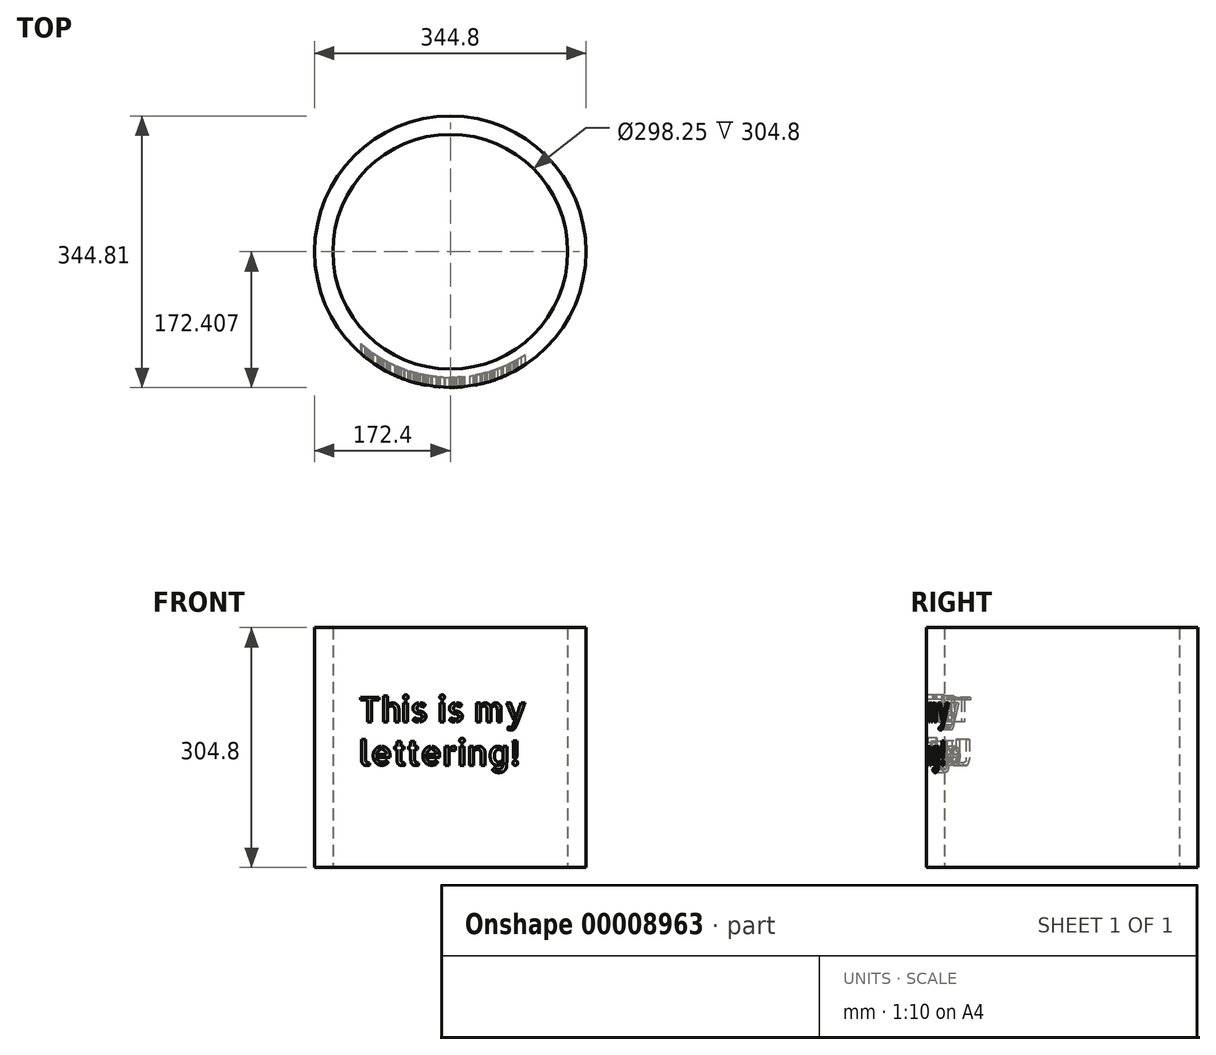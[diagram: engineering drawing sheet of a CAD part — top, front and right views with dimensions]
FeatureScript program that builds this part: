
annotation { "Feature Type Name" : "Feature", "Feature Type Description" : "" }
export const myFeature = defineFeature(function(context is Context, id is Id, definition is map)
    precondition{}
    {
        {
            var Q0;
            Q0=qCreatedBy(makeId("Top.planeOp"),FACE);
            var sketch = newSketch(context, id + "F0", { "sketchPlane" : qUnion([Q0])});
            skCircle(sketch, "E0", {"center": v(0, 214.13) * mm, "radius": 172.4 * mm});
            skCircle(sketch, "E1", {"center": v(0, 214.13) * mm, "radius": 149.13 * mm});
            skSolve(sketch);
        }
        {
            var Q0;
            Q0=makeQuery(id+"F0.imprint","IMPRINT",FACE,{"disambiguationData":[TD([[makeQuery(id+"F0.imprint","IMPRINT",EDGE,{"derivedFrom":sQuery(id+"F0.wireOp",EDGE,"E0")}),1.0]])]});
            extrude(context, id + "F1", {"entities" : qUnion([Q0]), "depth" : 304.8 * mm});
        }
        {
            var Q0;
            Q0=qCreatedBy(makeId("Front.planeOp"),FACE);
            var sketch = newSketch(context, id + "F2", { "sketchPlane" : qUnion([Q0])});
            skText(sketch, "E2", { "text": "This is my \nlettering!", "fontName": "AllertaStencil-Regular.ttf"});
            const initialGuessF2  = {"E2": [-0.11626, 0.18507, 1, 0, 0.031]};
            skSetInitialGuess(sketch, initialGuessF2);
            skSolve(sketch);
        }
        {
            var Q0;
            Q0 = qSketchRegion(id + "F2", true);
            var Q1;
            Q1=makeQuery(id+"F1.opExtrude","SWEPT_FACE",FACE,{"disambiguationData":[OSD([sQuery(id+"F0.wireOp",EDGE,"E0")])]});
            extrude(context, id + "F3", {"entities" : qUnion([Q0]), "endBound" : BoundingType.UP_TO_SURFACE, "oppositeDirection" : true, "endBoundEntityFace" : qUnion([Q1]), "depth" : 25.4 * mm});
        }
        {
            var Q0;
            Q0=makeQuery(id+"F3.opExtrude","SWEPT_BODY",BODY,{"disambiguationData":[OSD([sQuery(id+"F2.wireOp",EDGE,"E2.sketch_text.stroke-0"),sQuery(id+"F2.wireOp",EDGE,"E2.sketch_text.stroke-1"),sQuery(id+"F2.wireOp",EDGE,"E2.sketch_text.stroke-2"),sQuery(id+"F2.wireOp",EDGE,"E2.sketch_text.stroke-3"),sQuery(id+"F2.wireOp",EDGE,"E2.sketch_text.stroke-4"),sQuery(id+"F2.wireOp",EDGE,"E2.sketch_text.stroke-5"),sQuery(id+"F2.wireOp",EDGE,"E2.sketch_text.stroke-6"),sQuery(id+"F2.wireOp",EDGE,"E2.sketch_text.stroke-7")])]});
            var Q1;
            Q1=makeQuery(id+"F3.opExtrude","SWEPT_BODY",BODY,{"disambiguationData":[OSD([sQuery(id+"F2.wireOp",EDGE,"E2.sketch_text.stroke-8"),sQuery(id+"F2.wireOp",EDGE,"E2.sketch_text.stroke-9"),sQuery(id+"F2.wireOp",EDGE,"E2.sketch_text.stroke-10"),sQuery(id+"F2.wireOp",EDGE,"E2.sketch_text.stroke-11")])]});
            var Q2;
            Q2=makeQuery(id+"F3.opExtrude","SWEPT_BODY",BODY,{"disambiguationData":[OSD([sQuery(id+"F2.wireOp",EDGE,"E2.sketch_text.stroke-12"),sQuery(id+"F2.wireOp",EDGE,"E2.sketch_text.stroke-13"),sQuery(id+"F2.wireOp",EDGE,"E2.sketch_text.stroke-14"),sQuery(id+"F2.wireOp",EDGE,"E2.sketch_text.stroke-15"),sQuery(id+"F2.wireOp",EDGE,"E2.sketch_text.stroke-16"),sQuery(id+"F2.wireOp",EDGE,"E2.sketch_text.stroke-17"),sQuery(id+"F2.wireOp",EDGE,"E2.sketch_text.stroke-18"),sQuery(id+"F2.wireOp",EDGE,"E2.sketch_text.stroke-19"),sQuery(id+"F2.wireOp",EDGE,"E2.sketch_text.stroke-20"),sQuery(id+"F2.wireOp",EDGE,"E2.sketch_text.stroke-21"),sQuery(id+"F2.wireOp",EDGE,"E2.sketch_text.stroke-22"),sQuery(id+"F2.wireOp",EDGE,"E2.sketch_text.stroke-23"),sQuery(id+"F2.wireOp",EDGE,"E2.sketch_text.stroke-24"),sQuery(id+"F2.wireOp",EDGE,"E2.sketch_text.stroke-25"),sQuery(id+"F2.wireOp",EDGE,"E2.sketch_text.stroke-26"),sQuery(id+"F2.wireOp",EDGE,"E2.sketch_text.stroke-27"),sQuery(id+"F2.wireOp",EDGE,"E2.sketch_text.stroke-28"),sQuery(id+"F2.wireOp",EDGE,"E2.sketch_text.stroke-29"),sQuery(id+"F2.wireOp",EDGE,"E2.sketch_text.stroke-30")])]});
            var Q3;
            Q3=makeQuery(id+"F3.opExtrude","SWEPT_BODY",BODY,{"disambiguationData":[OSD([sQuery(id+"F2.wireOp",EDGE,"E2.sketch_text.stroke-31"),sQuery(id+"F2.wireOp",EDGE,"E2.sketch_text.stroke-32"),sQuery(id+"F2.wireOp",EDGE,"E2.sketch_text.stroke-33"),sQuery(id+"F2.wireOp",EDGE,"E2.sketch_text.stroke-34")])]});
            var Q4;
            Q4=makeQuery(id+"F3.opExtrude","SWEPT_BODY",BODY,{"disambiguationData":[OSD([sQuery(id+"F2.wireOp",EDGE,"E2.sketch_text.stroke-35"),sQuery(id+"F2.wireOp",EDGE,"E2.sketch_text.stroke-36"),sQuery(id+"F2.wireOp",EDGE,"E2.sketch_text.stroke-37"),sQuery(id+"F2.wireOp",EDGE,"E2.sketch_text.stroke-38"),sQuery(id+"F2.wireOp",EDGE,"E2.sketch_text.stroke-39"),sQuery(id+"F2.wireOp",EDGE,"E2.sketch_text.stroke-40"),sQuery(id+"F2.wireOp",EDGE,"E2.sketch_text.stroke-41"),sQuery(id+"F2.wireOp",EDGE,"E2.sketch_text.stroke-42")])]});
            var Q5;
            Q5=makeQuery(id+"F3.opExtrude","SWEPT_BODY",BODY,{"disambiguationData":[OSD([sQuery(id+"F2.wireOp",EDGE,"E2.sketch_text.stroke-43"),sQuery(id+"F2.wireOp",EDGE,"E2.sketch_text.stroke-44"),sQuery(id+"F2.wireOp",EDGE,"E2.sketch_text.stroke-45"),sQuery(id+"F2.wireOp",EDGE,"E2.sketch_text.stroke-46"),sQuery(id+"F2.wireOp",EDGE,"E2.sketch_text.stroke-47"),sQuery(id+"F2.wireOp",EDGE,"E2.sketch_text.stroke-48"),sQuery(id+"F2.wireOp",EDGE,"E2.sketch_text.stroke-49"),sQuery(id+"F2.wireOp",EDGE,"E2.sketch_text.stroke-50"),sQuery(id+"F2.wireOp",EDGE,"E2.sketch_text.stroke-51"),sQuery(id+"F2.wireOp",EDGE,"E2.sketch_text.stroke-52"),sQuery(id+"F2.wireOp",EDGE,"E2.sketch_text.stroke-53"),sQuery(id+"F2.wireOp",EDGE,"E2.sketch_text.stroke-54"),sQuery(id+"F2.wireOp",EDGE,"E2.sketch_text.stroke-55"),sQuery(id+"F2.wireOp",EDGE,"E2.sketch_text.stroke-56")])]});
            var Q6;
            Q6=makeQuery(id+"F3.opExtrude","SWEPT_BODY",BODY,{"disambiguationData":[OSD([sQuery(id+"F2.wireOp",EDGE,"E2.sketch_text.stroke-57"),sQuery(id+"F2.wireOp",EDGE,"E2.sketch_text.stroke-58"),sQuery(id+"F2.wireOp",EDGE,"E2.sketch_text.stroke-59"),sQuery(id+"F2.wireOp",EDGE,"E2.sketch_text.stroke-60"),sQuery(id+"F2.wireOp",EDGE,"E2.sketch_text.stroke-61"),sQuery(id+"F2.wireOp",EDGE,"E2.sketch_text.stroke-62")])]});
            var Q7;
            Q7=makeQuery(id+"F3.opExtrude","SWEPT_BODY",BODY,{"disambiguationData":[OSD([sQuery(id+"F2.wireOp",EDGE,"E2.sketch_text.stroke-63"),sQuery(id+"F2.wireOp",EDGE,"E2.sketch_text.stroke-64"),sQuery(id+"F2.wireOp",EDGE,"E2.sketch_text.stroke-65"),sQuery(id+"F2.wireOp",EDGE,"E2.sketch_text.stroke-66"),sQuery(id+"F2.wireOp",EDGE,"E2.sketch_text.stroke-67"),sQuery(id+"F2.wireOp",EDGE,"E2.sketch_text.stroke-68"),sQuery(id+"F2.wireOp",EDGE,"E2.sketch_text.stroke-69"),sQuery(id+"F2.wireOp",EDGE,"E2.sketch_text.stroke-70"),sQuery(id+"F2.wireOp",EDGE,"E2.sketch_text.stroke-71")])]});
            var Q8;
            Q8=makeQuery(id+"F3.opExtrude","SWEPT_BODY",BODY,{"disambiguationData":[OSD([sQuery(id+"F2.wireOp",EDGE,"E2.sketch_text.stroke-72"),sQuery(id+"F2.wireOp",EDGE,"E2.sketch_text.stroke-73"),sQuery(id+"F2.wireOp",EDGE,"E2.sketch_text.stroke-74"),sQuery(id+"F2.wireOp",EDGE,"E2.sketch_text.stroke-75"),sQuery(id+"F2.wireOp",EDGE,"E2.sketch_text.stroke-76"),sQuery(id+"F2.wireOp",EDGE,"E2.sketch_text.stroke-77"),sQuery(id+"F2.wireOp",EDGE,"E2.sketch_text.stroke-78"),sQuery(id+"F2.wireOp",EDGE,"E2.sketch_text.stroke-79"),sQuery(id+"F2.wireOp",EDGE,"E2.sketch_text.stroke-80"),sQuery(id+"F2.wireOp",EDGE,"E2.sketch_text.stroke-81"),sQuery(id+"F2.wireOp",EDGE,"E2.sketch_text.stroke-82"),sQuery(id+"F2.wireOp",EDGE,"E2.sketch_text.stroke-83"),sQuery(id+"F2.wireOp",EDGE,"E2.sketch_text.stroke-84"),sQuery(id+"F2.wireOp",EDGE,"E2.sketch_text.stroke-85")])]});
            var Q9;
            Q9=makeQuery(id+"F3.opExtrude","SWEPT_BODY",BODY,{"disambiguationData":[OSD([sQuery(id+"F2.wireOp",EDGE,"E2.sketch_text.stroke-86"),sQuery(id+"F2.wireOp",EDGE,"E2.sketch_text.stroke-87"),sQuery(id+"F2.wireOp",EDGE,"E2.sketch_text.stroke-88"),sQuery(id+"F2.wireOp",EDGE,"E2.sketch_text.stroke-89")])]});
            var Q10;
            Q10=makeQuery(id+"F3.opExtrude","SWEPT_BODY",BODY,{"disambiguationData":[OSD([sQuery(id+"F2.wireOp",EDGE,"E2.sketch_text.stroke-90"),sQuery(id+"F2.wireOp",EDGE,"E2.sketch_text.stroke-91"),sQuery(id+"F2.wireOp",EDGE,"E2.sketch_text.stroke-92"),sQuery(id+"F2.wireOp",EDGE,"E2.sketch_text.stroke-93"),sQuery(id+"F2.wireOp",EDGE,"E2.sketch_text.stroke-94"),sQuery(id+"F2.wireOp",EDGE,"E2.sketch_text.stroke-95"),sQuery(id+"F2.wireOp",EDGE,"E2.sketch_text.stroke-96"),sQuery(id+"F2.wireOp",EDGE,"E2.sketch_text.stroke-97")])]});
            var Q11;
            Q11=makeQuery(id+"F3.opExtrude","SWEPT_BODY",BODY,{"disambiguationData":[OSD([sQuery(id+"F2.wireOp",EDGE,"E2.sketch_text.stroke-98"),sQuery(id+"F2.wireOp",EDGE,"E2.sketch_text.stroke-99"),sQuery(id+"F2.wireOp",EDGE,"E2.sketch_text.stroke-100"),sQuery(id+"F2.wireOp",EDGE,"E2.sketch_text.stroke-101"),sQuery(id+"F2.wireOp",EDGE,"E2.sketch_text.stroke-102"),sQuery(id+"F2.wireOp",EDGE,"E2.sketch_text.stroke-103"),sQuery(id+"F2.wireOp",EDGE,"E2.sketch_text.stroke-104"),sQuery(id+"F2.wireOp",EDGE,"E2.sketch_text.stroke-105"),sQuery(id+"F2.wireOp",EDGE,"E2.sketch_text.stroke-106"),sQuery(id+"F2.wireOp",EDGE,"E2.sketch_text.stroke-107"),sQuery(id+"F2.wireOp",EDGE,"E2.sketch_text.stroke-108"),sQuery(id+"F2.wireOp",EDGE,"E2.sketch_text.stroke-109"),sQuery(id+"F2.wireOp",EDGE,"E2.sketch_text.stroke-110"),sQuery(id+"F2.wireOp",EDGE,"E2.sketch_text.stroke-111")])]});
            var Q12;
            Q12=makeQuery(id+"F3.opExtrude","SWEPT_BODY",BODY,{"disambiguationData":[OSD([sQuery(id+"F2.wireOp",EDGE,"E2.sketch_text.stroke-112"),sQuery(id+"F2.wireOp",EDGE,"E2.sketch_text.stroke-113"),sQuery(id+"F2.wireOp",EDGE,"E2.sketch_text.stroke-114"),sQuery(id+"F2.wireOp",EDGE,"E2.sketch_text.stroke-115"),sQuery(id+"F2.wireOp",EDGE,"E2.sketch_text.stroke-116"),sQuery(id+"F2.wireOp",EDGE,"E2.sketch_text.stroke-117")])]});
            var Q13;
            Q13=makeQuery(id+"F3.opExtrude","SWEPT_BODY",BODY,{"disambiguationData":[OSD([sQuery(id+"F2.wireOp",EDGE,"E2.sketch_text.stroke-118"),sQuery(id+"F2.wireOp",EDGE,"E2.sketch_text.stroke-119"),sQuery(id+"F2.wireOp",EDGE,"E2.sketch_text.stroke-120"),sQuery(id+"F2.wireOp",EDGE,"E2.sketch_text.stroke-121"),sQuery(id+"F2.wireOp",EDGE,"E2.sketch_text.stroke-122"),sQuery(id+"F2.wireOp",EDGE,"E2.sketch_text.stroke-123"),sQuery(id+"F2.wireOp",EDGE,"E2.sketch_text.stroke-124"),sQuery(id+"F2.wireOp",EDGE,"E2.sketch_text.stroke-125"),sQuery(id+"F2.wireOp",EDGE,"E2.sketch_text.stroke-126")])]});
            var Q14;
            Q14=makeQuery(id+"F3.opExtrude","SWEPT_BODY",BODY,{"disambiguationData":[OSD([sQuery(id+"F2.wireOp",EDGE,"E2.sketch_text.stroke-127"),sQuery(id+"F2.wireOp",EDGE,"E2.sketch_text.stroke-128"),sQuery(id+"F2.wireOp",EDGE,"E2.sketch_text.stroke-129"),sQuery(id+"F2.wireOp",EDGE,"E2.sketch_text.stroke-130"),sQuery(id+"F2.wireOp",EDGE,"E2.sketch_text.stroke-131"),sQuery(id+"F2.wireOp",EDGE,"E2.sketch_text.stroke-132"),sQuery(id+"F2.wireOp",EDGE,"E2.sketch_text.stroke-133"),sQuery(id+"F2.wireOp",EDGE,"E2.sketch_text.stroke-134"),sQuery(id+"F2.wireOp",EDGE,"E2.sketch_text.stroke-135"),sQuery(id+"F2.wireOp",EDGE,"E2.sketch_text.stroke-136"),sQuery(id+"F2.wireOp",EDGE,"E2.sketch_text.stroke-137"),sQuery(id+"F2.wireOp",EDGE,"E2.sketch_text.stroke-138"),sQuery(id+"F2.wireOp",EDGE,"E2.sketch_text.stroke-139"),sQuery(id+"F2.wireOp",EDGE,"E2.sketch_text.stroke-140")])]});
            var Q15;
            Q15=makeQuery(id+"F3.opExtrude","SWEPT_BODY",BODY,{"disambiguationData":[OSD([sQuery(id+"F2.wireOp",EDGE,"E2.sketch_text.stroke-141"),sQuery(id+"F2.wireOp",EDGE,"E2.sketch_text.stroke-142"),sQuery(id+"F2.wireOp",EDGE,"E2.sketch_text.stroke-143"),sQuery(id+"F2.wireOp",EDGE,"E2.sketch_text.stroke-144"),sQuery(id+"F2.wireOp",EDGE,"E2.sketch_text.stroke-145")])]});
            var Q16;
            Q16=makeQuery(id+"F3.opExtrude","SWEPT_BODY",BODY,{"disambiguationData":[OSD([sQuery(id+"F2.wireOp",EDGE,"E2.sketch_text.stroke-146"),sQuery(id+"F2.wireOp",EDGE,"E2.sketch_text.stroke-147"),sQuery(id+"F2.wireOp",EDGE,"E2.sketch_text.stroke-148"),sQuery(id+"F2.wireOp",EDGE,"E2.sketch_text.stroke-149"),sQuery(id+"F2.wireOp",EDGE,"E2.sketch_text.stroke-150"),sQuery(id+"F2.wireOp",EDGE,"E2.sketch_text.stroke-151"),sQuery(id+"F2.wireOp",EDGE,"E2.sketch_text.stroke-152"),sQuery(id+"F2.wireOp",EDGE,"E2.sketch_text.stroke-153"),sQuery(id+"F2.wireOp",EDGE,"E2.sketch_text.stroke-154"),sQuery(id+"F2.wireOp",EDGE,"E2.sketch_text.stroke-155"),sQuery(id+"F2.wireOp",EDGE,"E2.sketch_text.stroke-156"),sQuery(id+"F2.wireOp",EDGE,"E2.sketch_text.stroke-157"),sQuery(id+"F2.wireOp",EDGE,"E2.sketch_text.stroke-158"),sQuery(id+"F2.wireOp",EDGE,"E2.sketch_text.stroke-159"),sQuery(id+"F2.wireOp",EDGE,"E2.sketch_text.stroke-160"),sQuery(id+"F2.wireOp",EDGE,"E2.sketch_text.stroke-161")])]});
            var Q17;
            Q17=makeQuery(id+"F3.opExtrude","SWEPT_BODY",BODY,{"disambiguationData":[OSD([sQuery(id+"F2.wireOp",EDGE,"E2.sketch_text.stroke-162"),sQuery(id+"F2.wireOp",EDGE,"E2.sketch_text.stroke-163"),sQuery(id+"F2.wireOp",EDGE,"E2.sketch_text.stroke-164"),sQuery(id+"F2.wireOp",EDGE,"E2.sketch_text.stroke-165"),sQuery(id+"F2.wireOp",EDGE,"E2.sketch_text.stroke-166"),sQuery(id+"F2.wireOp",EDGE,"E2.sketch_text.stroke-167"),sQuery(id+"F2.wireOp",EDGE,"E2.sketch_text.stroke-168"),sQuery(id+"F2.wireOp",EDGE,"E2.sketch_text.stroke-169"),sQuery(id+"F2.wireOp",EDGE,"E2.sketch_text.stroke-170"),sQuery(id+"F2.wireOp",EDGE,"E2.sketch_text.stroke-171"),sQuery(id+"F2.wireOp",EDGE,"E2.sketch_text.stroke-172"),sQuery(id+"F2.wireOp",EDGE,"E2.sketch_text.stroke-173"),sQuery(id+"F2.wireOp",EDGE,"E2.sketch_text.stroke-174"),sQuery(id+"F2.wireOp",EDGE,"E2.sketch_text.stroke-175"),sQuery(id+"F2.wireOp",EDGE,"E2.sketch_text.stroke-176"),sQuery(id+"F2.wireOp",EDGE,"E2.sketch_text.stroke-177"),sQuery(id+"F2.wireOp",EDGE,"E2.sketch_text.stroke-178"),sQuery(id+"F2.wireOp",EDGE,"E2.sketch_text.stroke-179")])]});
            var Q18;
            Q18=makeQuery(id+"F3.opExtrude","SWEPT_BODY",BODY,{"disambiguationData":[OSD([sQuery(id+"F2.wireOp",EDGE,"E2.sketch_text.stroke-180"),sQuery(id+"F2.wireOp",EDGE,"E2.sketch_text.stroke-181"),sQuery(id+"F2.wireOp",EDGE,"E2.sketch_text.stroke-182"),sQuery(id+"F2.wireOp",EDGE,"E2.sketch_text.stroke-183"),sQuery(id+"F2.wireOp",EDGE,"E2.sketch_text.stroke-184"),sQuery(id+"F2.wireOp",EDGE,"E2.sketch_text.stroke-185"),sQuery(id+"F2.wireOp",EDGE,"E2.sketch_text.stroke-186"),sQuery(id+"F2.wireOp",EDGE,"E2.sketch_text.stroke-187"),sQuery(id+"F2.wireOp",EDGE,"E2.sketch_text.stroke-188"),sQuery(id+"F2.wireOp",EDGE,"E2.sketch_text.stroke-189"),sQuery(id+"F2.wireOp",EDGE,"E2.sketch_text.stroke-190"),sQuery(id+"F2.wireOp",EDGE,"E2.sketch_text.stroke-191"),sQuery(id+"F2.wireOp",EDGE,"E2.sketch_text.stroke-192"),sQuery(id+"F2.wireOp",EDGE,"E2.sketch_text.stroke-193"),sQuery(id+"F2.wireOp",EDGE,"E2.sketch_text.stroke-194"),sQuery(id+"F2.wireOp",EDGE,"E2.sketch_text.stroke-195"),sQuery(id+"F2.wireOp",EDGE,"E2.sketch_text.stroke-196"),sQuery(id+"F2.wireOp",EDGE,"E2.sketch_text.stroke-197"),sQuery(id+"F2.wireOp",EDGE,"E2.sketch_text.stroke-198"),sQuery(id+"F2.wireOp",EDGE,"E2.sketch_text.stroke-199"),sQuery(id+"F2.wireOp",EDGE,"E2.sketch_text.stroke-200"),sQuery(id+"F2.wireOp",EDGE,"E2.sketch_text.stroke-201"),sQuery(id+"F2.wireOp",EDGE,"E2.sketch_text.stroke-202"),sQuery(id+"F2.wireOp",EDGE,"E2.sketch_text.stroke-203")])]});
            var Q19;
            Q19=makeQuery(id+"F3.opExtrude","SWEPT_BODY",BODY,{"disambiguationData":[OSD([sQuery(id+"F2.wireOp",EDGE,"E2.sketch_text.stroke-204"),sQuery(id+"F2.wireOp",EDGE,"E2.sketch_text.stroke-205"),sQuery(id+"F2.wireOp",EDGE,"E2.sketch_text.stroke-206"),sQuery(id+"F2.wireOp",EDGE,"E2.sketch_text.stroke-207"),sQuery(id+"F2.wireOp",EDGE,"E2.sketch_text.stroke-208")])]});
            var Q20;
            Q20=makeQuery(id+"F3.opExtrude","SWEPT_BODY",BODY,{"disambiguationData":[OSD([sQuery(id+"F2.wireOp",EDGE,"E2.sketch_text.stroke-209"),sQuery(id+"F2.wireOp",EDGE,"E2.sketch_text.stroke-210"),sQuery(id+"F2.wireOp",EDGE,"E2.sketch_text.stroke-211"),sQuery(id+"F2.wireOp",EDGE,"E2.sketch_text.stroke-212"),sQuery(id+"F2.wireOp",EDGE,"E2.sketch_text.stroke-213"),sQuery(id+"F2.wireOp",EDGE,"E2.sketch_text.stroke-214"),sQuery(id+"F2.wireOp",EDGE,"E2.sketch_text.stroke-215"),sQuery(id+"F2.wireOp",EDGE,"E2.sketch_text.stroke-216"),sQuery(id+"F2.wireOp",EDGE,"E2.sketch_text.stroke-217"),sQuery(id+"F2.wireOp",EDGE,"E2.sketch_text.stroke-218"),sQuery(id+"F2.wireOp",EDGE,"E2.sketch_text.stroke-219"),sQuery(id+"F2.wireOp",EDGE,"E2.sketch_text.stroke-220"),sQuery(id+"F2.wireOp",EDGE,"E2.sketch_text.stroke-221"),sQuery(id+"F2.wireOp",EDGE,"E2.sketch_text.stroke-222"),sQuery(id+"F2.wireOp",EDGE,"E2.sketch_text.stroke-223"),sQuery(id+"F2.wireOp",EDGE,"E2.sketch_text.stroke-224"),sQuery(id+"F2.wireOp",EDGE,"E2.sketch_text.stroke-225"),sQuery(id+"F2.wireOp",EDGE,"E2.sketch_text.stroke-226")])]});
            var Q21;
            Q21=makeQuery(id+"F3.opExtrude","SWEPT_BODY",BODY,{"disambiguationData":[OSD([sQuery(id+"F2.wireOp",EDGE,"E2.sketch_text.stroke-227"),sQuery(id+"F2.wireOp",EDGE,"E2.sketch_text.stroke-228"),sQuery(id+"F2.wireOp",EDGE,"E2.sketch_text.stroke-229"),sQuery(id+"F2.wireOp",EDGE,"E2.sketch_text.stroke-230"),sQuery(id+"F2.wireOp",EDGE,"E2.sketch_text.stroke-231"),sQuery(id+"F2.wireOp",EDGE,"E2.sketch_text.stroke-232"),sQuery(id+"F2.wireOp",EDGE,"E2.sketch_text.stroke-233"),sQuery(id+"F2.wireOp",EDGE,"E2.sketch_text.stroke-234"),sQuery(id+"F2.wireOp",EDGE,"E2.sketch_text.stroke-235"),sQuery(id+"F2.wireOp",EDGE,"E2.sketch_text.stroke-236"),sQuery(id+"F2.wireOp",EDGE,"E2.sketch_text.stroke-237"),sQuery(id+"F2.wireOp",EDGE,"E2.sketch_text.stroke-238"),sQuery(id+"F2.wireOp",EDGE,"E2.sketch_text.stroke-239")])]});
            var Q22;
            Q22=makeQuery(id+"F3.opExtrude","SWEPT_BODY",BODY,{"disambiguationData":[OSD([sQuery(id+"F2.wireOp",EDGE,"E2.sketch_text.stroke-240"),sQuery(id+"F2.wireOp",EDGE,"E2.sketch_text.stroke-241"),sQuery(id+"F2.wireOp",EDGE,"E2.sketch_text.stroke-242"),sQuery(id+"F2.wireOp",EDGE,"E2.sketch_text.stroke-243"),sQuery(id+"F2.wireOp",EDGE,"E2.sketch_text.stroke-244"),sQuery(id+"F2.wireOp",EDGE,"E2.sketch_text.stroke-245"),sQuery(id+"F2.wireOp",EDGE,"E2.sketch_text.stroke-246"),sQuery(id+"F2.wireOp",EDGE,"E2.sketch_text.stroke-247"),sQuery(id+"F2.wireOp",EDGE,"E2.sketch_text.stroke-248"),sQuery(id+"F2.wireOp",EDGE,"E2.sketch_text.stroke-249"),sQuery(id+"F2.wireOp",EDGE,"E2.sketch_text.stroke-250"),sQuery(id+"F2.wireOp",EDGE,"E2.sketch_text.stroke-251"),sQuery(id+"F2.wireOp",EDGE,"E2.sketch_text.stroke-252"),sQuery(id+"F2.wireOp",EDGE,"E2.sketch_text.stroke-253"),sQuery(id+"F2.wireOp",EDGE,"E2.sketch_text.stroke-254"),sQuery(id+"F2.wireOp",EDGE,"E2.sketch_text.stroke-255"),sQuery(id+"F2.wireOp",EDGE,"E2.sketch_text.stroke-256"),sQuery(id+"F2.wireOp",EDGE,"E2.sketch_text.stroke-257"),sQuery(id+"F2.wireOp",EDGE,"E2.sketch_text.stroke-258"),sQuery(id+"F2.wireOp",EDGE,"E2.sketch_text.stroke-259"),sQuery(id+"F2.wireOp",EDGE,"E2.sketch_text.stroke-260"),sQuery(id+"F2.wireOp",EDGE,"E2.sketch_text.stroke-261"),sQuery(id+"F2.wireOp",EDGE,"E2.sketch_text.stroke-262"),sQuery(id+"F2.wireOp",EDGE,"E2.sketch_text.stroke-263")])]});
            var Q23;
            Q23=makeQuery(id+"F3.opExtrude","SWEPT_BODY",BODY,{"disambiguationData":[OSD([sQuery(id+"F2.wireOp",EDGE,"E2.sketch_text.stroke-264"),sQuery(id+"F2.wireOp",EDGE,"E2.sketch_text.stroke-265"),sQuery(id+"F2.wireOp",EDGE,"E2.sketch_text.stroke-266"),sQuery(id+"F2.wireOp",EDGE,"E2.sketch_text.stroke-267"),sQuery(id+"F2.wireOp",EDGE,"E2.sketch_text.stroke-268"),sQuery(id+"F2.wireOp",EDGE,"E2.sketch_text.stroke-269"),sQuery(id+"F2.wireOp",EDGE,"E2.sketch_text.stroke-270"),sQuery(id+"F2.wireOp",EDGE,"E2.sketch_text.stroke-271"),sQuery(id+"F2.wireOp",EDGE,"E2.sketch_text.stroke-272"),sQuery(id+"F2.wireOp",EDGE,"E2.sketch_text.stroke-273"),sQuery(id+"F2.wireOp",EDGE,"E2.sketch_text.stroke-274"),sQuery(id+"F2.wireOp",EDGE,"E2.sketch_text.stroke-275"),sQuery(id+"F2.wireOp",EDGE,"E2.sketch_text.stroke-276"),sQuery(id+"F2.wireOp",EDGE,"E2.sketch_text.stroke-277"),sQuery(id+"F2.wireOp",EDGE,"E2.sketch_text.stroke-278"),sQuery(id+"F2.wireOp",EDGE,"E2.sketch_text.stroke-279"),sQuery(id+"F2.wireOp",EDGE,"E2.sketch_text.stroke-280"),sQuery(id+"F2.wireOp",EDGE,"E2.sketch_text.stroke-281"),sQuery(id+"F2.wireOp",EDGE,"E2.sketch_text.stroke-282"),sQuery(id+"F2.wireOp",EDGE,"E2.sketch_text.stroke-283"),sQuery(id+"F2.wireOp",EDGE,"E2.sketch_text.stroke-284"),sQuery(id+"F2.wireOp",EDGE,"E2.sketch_text.stroke-285"),sQuery(id+"F2.wireOp",EDGE,"E2.sketch_text.stroke-286"),sQuery(id+"F2.wireOp",EDGE,"E2.sketch_text.stroke-287"),sQuery(id+"F2.wireOp",EDGE,"E2.sketch_text.stroke-288")])]});
            var Q24;
            Q24=makeQuery(id+"F3.opExtrude","SWEPT_BODY",BODY,{"disambiguationData":[OSD([sQuery(id+"F2.wireOp",EDGE,"E2.sketch_text.stroke-289"),sQuery(id+"F2.wireOp",EDGE,"E2.sketch_text.stroke-290"),sQuery(id+"F2.wireOp",EDGE,"E2.sketch_text.stroke-291"),sQuery(id+"F2.wireOp",EDGE,"E2.sketch_text.stroke-292"),sQuery(id+"F2.wireOp",EDGE,"E2.sketch_text.stroke-293"),sQuery(id+"F2.wireOp",EDGE,"E2.sketch_text.stroke-294"),sQuery(id+"F2.wireOp",EDGE,"E2.sketch_text.stroke-295"),sQuery(id+"F2.wireOp",EDGE,"E2.sketch_text.stroke-296"),sQuery(id+"F2.wireOp",EDGE,"E2.sketch_text.stroke-297"),sQuery(id+"F2.wireOp",EDGE,"E2.sketch_text.stroke-298"),sQuery(id+"F2.wireOp",EDGE,"E2.sketch_text.stroke-299"),sQuery(id+"F2.wireOp",EDGE,"E2.sketch_text.stroke-300"),sQuery(id+"F2.wireOp",EDGE,"E2.sketch_text.stroke-301"),sQuery(id+"F2.wireOp",EDGE,"E2.sketch_text.stroke-302"),sQuery(id+"F2.wireOp",EDGE,"E2.sketch_text.stroke-303"),sQuery(id+"F2.wireOp",EDGE,"E2.sketch_text.stroke-304"),sQuery(id+"F2.wireOp",EDGE,"E2.sketch_text.stroke-305"),sQuery(id+"F2.wireOp",EDGE,"E2.sketch_text.stroke-306"),sQuery(id+"F2.wireOp",EDGE,"E2.sketch_text.stroke-307"),sQuery(id+"F2.wireOp",EDGE,"E2.sketch_text.stroke-308"),sQuery(id+"F2.wireOp",EDGE,"E2.sketch_text.stroke-309"),sQuery(id+"F2.wireOp",EDGE,"E2.sketch_text.stroke-310"),sQuery(id+"F2.wireOp",EDGE,"E2.sketch_text.stroke-311"),sQuery(id+"F2.wireOp",EDGE,"E2.sketch_text.stroke-312"),sQuery(id+"F2.wireOp",EDGE,"E2.sketch_text.stroke-313")])]});
            var Q25;
            Q25=makeQuery(id+"F3.opExtrude","SWEPT_BODY",BODY,{"disambiguationData":[OSD([sQuery(id+"F2.wireOp",EDGE,"E2.sketch_text.stroke-314"),sQuery(id+"F2.wireOp",EDGE,"E2.sketch_text.stroke-315"),sQuery(id+"F2.wireOp",EDGE,"E2.sketch_text.stroke-316"),sQuery(id+"F2.wireOp",EDGE,"E2.sketch_text.stroke-317"),sQuery(id+"F2.wireOp",EDGE,"E2.sketch_text.stroke-318"),sQuery(id+"F2.wireOp",EDGE,"E2.sketch_text.stroke-319"),sQuery(id+"F2.wireOp",EDGE,"E2.sketch_text.stroke-320"),sQuery(id+"F2.wireOp",EDGE,"E2.sketch_text.stroke-321"),sQuery(id+"F2.wireOp",EDGE,"E2.sketch_text.stroke-322"),sQuery(id+"F2.wireOp",EDGE,"E2.sketch_text.stroke-323"),sQuery(id+"F2.wireOp",EDGE,"E2.sketch_text.stroke-324"),sQuery(id+"F2.wireOp",EDGE,"E2.sketch_text.stroke-325"),sQuery(id+"F2.wireOp",EDGE,"E2.sketch_text.stroke-326")])]});
            var Q26;
            Q26=makeQuery(id+"F3.opExtrude","SWEPT_BODY",BODY,{"disambiguationData":[OSD([sQuery(id+"F2.wireOp",EDGE,"E2.sketch_text.stroke-327"),sQuery(id+"F2.wireOp",EDGE,"E2.sketch_text.stroke-328"),sQuery(id+"F2.wireOp",EDGE,"E2.sketch_text.stroke-329"),sQuery(id+"F2.wireOp",EDGE,"E2.sketch_text.stroke-330"),sQuery(id+"F2.wireOp",EDGE,"E2.sketch_text.stroke-331"),sQuery(id+"F2.wireOp",EDGE,"E2.sketch_text.stroke-332"),sQuery(id+"F2.wireOp",EDGE,"E2.sketch_text.stroke-333"),sQuery(id+"F2.wireOp",EDGE,"E2.sketch_text.stroke-334"),sQuery(id+"F2.wireOp",EDGE,"E2.sketch_text.stroke-335"),sQuery(id+"F2.wireOp",EDGE,"E2.sketch_text.stroke-336"),sQuery(id+"F2.wireOp",EDGE,"E2.sketch_text.stroke-337"),sQuery(id+"F2.wireOp",EDGE,"E2.sketch_text.stroke-338"),sQuery(id+"F2.wireOp",EDGE,"E2.sketch_text.stroke-339"),sQuery(id+"F2.wireOp",EDGE,"E2.sketch_text.stroke-340"),sQuery(id+"F2.wireOp",EDGE,"E2.sketch_text.stroke-341"),sQuery(id+"F2.wireOp",EDGE,"E2.sketch_text.stroke-342"),sQuery(id+"F2.wireOp",EDGE,"E2.sketch_text.stroke-343"),sQuery(id+"F2.wireOp",EDGE,"E2.sketch_text.stroke-344"),sQuery(id+"F2.wireOp",EDGE,"E2.sketch_text.stroke-345"),sQuery(id+"F2.wireOp",EDGE,"E2.sketch_text.stroke-346"),sQuery(id+"F2.wireOp",EDGE,"E2.sketch_text.stroke-347"),sQuery(id+"F2.wireOp",EDGE,"E2.sketch_text.stroke-348"),sQuery(id+"F2.wireOp",EDGE,"E2.sketch_text.stroke-349"),sQuery(id+"F2.wireOp",EDGE,"E2.sketch_text.stroke-350")])]});
            var Q27;
            Q27=makeQuery(id+"F3.opExtrude","SWEPT_BODY",BODY,{"disambiguationData":[OSD([sQuery(id+"F2.wireOp",EDGE,"E2.sketch_text.stroke-351"),sQuery(id+"F2.wireOp",EDGE,"E2.sketch_text.stroke-352"),sQuery(id+"F2.wireOp",EDGE,"E2.sketch_text.stroke-353"),sQuery(id+"F2.wireOp",EDGE,"E2.sketch_text.stroke-354"),sQuery(id+"F2.wireOp",EDGE,"E2.sketch_text.stroke-355"),sQuery(id+"F2.wireOp",EDGE,"E2.sketch_text.stroke-356"),sQuery(id+"F2.wireOp",EDGE,"E2.sketch_text.stroke-357")])]});
            var Q28;
            Q28=makeQuery(id+"F3.opExtrude","SWEPT_BODY",BODY,{"disambiguationData":[OSD([sQuery(id+"F2.wireOp",EDGE,"E2.sketch_text.stroke-358"),sQuery(id+"F2.wireOp",EDGE,"E2.sketch_text.stroke-359"),sQuery(id+"F2.wireOp",EDGE,"E2.sketch_text.stroke-360"),sQuery(id+"F2.wireOp",EDGE,"E2.sketch_text.stroke-361"),sQuery(id+"F2.wireOp",EDGE,"E2.sketch_text.stroke-362"),sQuery(id+"F2.wireOp",EDGE,"E2.sketch_text.stroke-363"),sQuery(id+"F2.wireOp",EDGE,"E2.sketch_text.stroke-364")])]});
            var Q29;
            Q29=makeQuery(id+"F3.opExtrude","SWEPT_BODY",BODY,{"disambiguationData":[OSD([sQuery(id+"F2.wireOp",EDGE,"E2.sketch_text.stroke-365"),sQuery(id+"F2.wireOp",EDGE,"E2.sketch_text.stroke-366"),sQuery(id+"F2.wireOp",EDGE,"E2.sketch_text.stroke-367"),sQuery(id+"F2.wireOp",EDGE,"E2.sketch_text.stroke-368")])]});
            var Q30;
            Q30=makeQuery(id+"F3.opExtrude","SWEPT_BODY",BODY,{"disambiguationData":[OSD([sQuery(id+"F2.wireOp",EDGE,"E2.sketch_text.stroke-369"),sQuery(id+"F2.wireOp",EDGE,"E2.sketch_text.stroke-370"),sQuery(id+"F2.wireOp",EDGE,"E2.sketch_text.stroke-371"),sQuery(id+"F2.wireOp",EDGE,"E2.sketch_text.stroke-372"),sQuery(id+"F2.wireOp",EDGE,"E2.sketch_text.stroke-373"),sQuery(id+"F2.wireOp",EDGE,"E2.sketch_text.stroke-374"),sQuery(id+"F2.wireOp",EDGE,"E2.sketch_text.stroke-375"),sQuery(id+"F2.wireOp",EDGE,"E2.sketch_text.stroke-376")])]});
            var Q31;
            Q31=makeQuery(id+"F3.opExtrude","SWEPT_BODY",BODY,{"disambiguationData":[OSD([sQuery(id+"F2.wireOp",EDGE,"E2.sketch_text.stroke-377"),sQuery(id+"F2.wireOp",EDGE,"E2.sketch_text.stroke-378"),sQuery(id+"F2.wireOp",EDGE,"E2.sketch_text.stroke-379"),sQuery(id+"F2.wireOp",EDGE,"E2.sketch_text.stroke-380"),sQuery(id+"F2.wireOp",EDGE,"E2.sketch_text.stroke-381")])]});
            var Q32;
            Q32=makeQuery(id+"F3.opExtrude","SWEPT_BODY",BODY,{"disambiguationData":[OSD([sQuery(id+"F2.wireOp",EDGE,"E2.sketch_text.stroke-382"),sQuery(id+"F2.wireOp",EDGE,"E2.sketch_text.stroke-383"),sQuery(id+"F2.wireOp",EDGE,"E2.sketch_text.stroke-384"),sQuery(id+"F2.wireOp",EDGE,"E2.sketch_text.stroke-385"),sQuery(id+"F2.wireOp",EDGE,"E2.sketch_text.stroke-386"),sQuery(id+"F2.wireOp",EDGE,"E2.sketch_text.stroke-387"),sQuery(id+"F2.wireOp",EDGE,"E2.sketch_text.stroke-388"),sQuery(id+"F2.wireOp",EDGE,"E2.sketch_text.stroke-389"),sQuery(id+"F2.wireOp",EDGE,"E2.sketch_text.stroke-390"),sQuery(id+"F2.wireOp",EDGE,"E2.sketch_text.stroke-391"),sQuery(id+"F2.wireOp",EDGE,"E2.sketch_text.stroke-392"),sQuery(id+"F2.wireOp",EDGE,"E2.sketch_text.stroke-393"),sQuery(id+"F2.wireOp",EDGE,"E2.sketch_text.stroke-394"),sQuery(id+"F2.wireOp",EDGE,"E2.sketch_text.stroke-395"),sQuery(id+"F2.wireOp",EDGE,"E2.sketch_text.stroke-396"),sQuery(id+"F2.wireOp",EDGE,"E2.sketch_text.stroke-397"),sQuery(id+"F2.wireOp",EDGE,"E2.sketch_text.stroke-398"),sQuery(id+"F2.wireOp",EDGE,"E2.sketch_text.stroke-399"),sQuery(id+"F2.wireOp",EDGE,"E2.sketch_text.stroke-400")])]});
            var Q33;
            Q33=makeQuery(id+"F3.opExtrude","SWEPT_BODY",BODY,{"disambiguationData":[OSD([sQuery(id+"F2.wireOp",EDGE,"E2.sketch_text.stroke-401"),sQuery(id+"F2.wireOp",EDGE,"E2.sketch_text.stroke-402"),sQuery(id+"F2.wireOp",EDGE,"E2.sketch_text.stroke-403"),sQuery(id+"F2.wireOp",EDGE,"E2.sketch_text.stroke-404"),sQuery(id+"F2.wireOp",EDGE,"E2.sketch_text.stroke-405"),sQuery(id+"F2.wireOp",EDGE,"E2.sketch_text.stroke-406"),sQuery(id+"F2.wireOp",EDGE,"E2.sketch_text.stroke-407"),sQuery(id+"F2.wireOp",EDGE,"E2.sketch_text.stroke-408"),sQuery(id+"F2.wireOp",EDGE,"E2.sketch_text.stroke-409"),sQuery(id+"F2.wireOp",EDGE,"E2.sketch_text.stroke-410"),sQuery(id+"F2.wireOp",EDGE,"E2.sketch_text.stroke-411"),sQuery(id+"F2.wireOp",EDGE,"E2.sketch_text.stroke-412"),sQuery(id+"F2.wireOp",EDGE,"E2.sketch_text.stroke-413"),sQuery(id+"F2.wireOp",EDGE,"E2.sketch_text.stroke-414"),sQuery(id+"F2.wireOp",EDGE,"E2.sketch_text.stroke-415"),sQuery(id+"F2.wireOp",EDGE,"E2.sketch_text.stroke-416"),sQuery(id+"F2.wireOp",EDGE,"E2.sketch_text.stroke-417"),sQuery(id+"F2.wireOp",EDGE,"E2.sketch_text.stroke-418"),sQuery(id+"F2.wireOp",EDGE,"E2.sketch_text.stroke-419"),sQuery(id+"F2.wireOp",EDGE,"E2.sketch_text.stroke-420"),sQuery(id+"F2.wireOp",EDGE,"E2.sketch_text.stroke-421"),sQuery(id+"F2.wireOp",EDGE,"E2.sketch_text.stroke-422"),sQuery(id+"F2.wireOp",EDGE,"E2.sketch_text.stroke-423"),sQuery(id+"F2.wireOp",EDGE,"E2.sketch_text.stroke-424"),sQuery(id+"F2.wireOp",EDGE,"E2.sketch_text.stroke-425"),sQuery(id+"F2.wireOp",EDGE,"E2.sketch_text.stroke-426")])]});
            var Q34;
            Q34=makeQuery(id+"F3.opExtrude","SWEPT_BODY",BODY,{"disambiguationData":[OSD([sQuery(id+"F2.wireOp",EDGE,"E2.sketch_text.stroke-427"),sQuery(id+"F2.wireOp",EDGE,"E2.sketch_text.stroke-428"),sQuery(id+"F2.wireOp",EDGE,"E2.sketch_text.stroke-429"),sQuery(id+"F2.wireOp",EDGE,"E2.sketch_text.stroke-430"),sQuery(id+"F2.wireOp",EDGE,"E2.sketch_text.stroke-431"),sQuery(id+"F2.wireOp",EDGE,"E2.sketch_text.stroke-432"),sQuery(id+"F2.wireOp",EDGE,"E2.sketch_text.stroke-433"),sQuery(id+"F2.wireOp",EDGE,"E2.sketch_text.stroke-434"),sQuery(id+"F2.wireOp",EDGE,"E2.sketch_text.stroke-435"),sQuery(id+"F2.wireOp",EDGE,"E2.sketch_text.stroke-436"),sQuery(id+"F2.wireOp",EDGE,"E2.sketch_text.stroke-437"),sQuery(id+"F2.wireOp",EDGE,"E2.sketch_text.stroke-438"),sQuery(id+"F2.wireOp",EDGE,"E2.sketch_text.stroke-439"),sQuery(id+"F2.wireOp",EDGE,"E2.sketch_text.stroke-440"),sQuery(id+"F2.wireOp",EDGE,"E2.sketch_text.stroke-441"),sQuery(id+"F2.wireOp",EDGE,"E2.sketch_text.stroke-442"),sQuery(id+"F2.wireOp",EDGE,"E2.sketch_text.stroke-443")])]});
            var Q35;
            Q35=makeQuery(id+"F3.opExtrude","SWEPT_BODY",BODY,{"disambiguationData":[OSD([sQuery(id+"F2.wireOp",EDGE,"E2.sketch_text.stroke-444"),sQuery(id+"F2.wireOp",EDGE,"E2.sketch_text.stroke-445"),sQuery(id+"F2.wireOp",EDGE,"E2.sketch_text.stroke-446"),sQuery(id+"F2.wireOp",EDGE,"E2.sketch_text.stroke-447")])]});
            var Q36;
            Q36=makeQuery(id+"F3.opExtrude","SWEPT_BODY",BODY,{"disambiguationData":[OSD([sQuery(id+"F2.wireOp",EDGE,"E2.sketch_text.stroke-448"),sQuery(id+"F2.wireOp",EDGE,"E2.sketch_text.stroke-449"),sQuery(id+"F2.wireOp",EDGE,"E2.sketch_text.stroke-450"),sQuery(id+"F2.wireOp",EDGE,"E2.sketch_text.stroke-451"),sQuery(id+"F2.wireOp",EDGE,"E2.sketch_text.stroke-452"),sQuery(id+"F2.wireOp",EDGE,"E2.sketch_text.stroke-453"),sQuery(id+"F2.wireOp",EDGE,"E2.sketch_text.stroke-454"),sQuery(id+"F2.wireOp",EDGE,"E2.sketch_text.stroke-455")])]});
            var Q37;
            Q37=qCreatedBy(makeId("Front.planeOp"),FACE);
            transform(context, id + "F4", {"entities" : qUnion([Q0, Q1, Q2, Q3, Q4, Q5, Q6, Q7, Q8, Q9, Q10, Q11, Q12, Q13, Q14, Q15, Q16, Q17, Q18, Q19, Q20, Q21, Q22, Q23, Q24, Q25, Q26, Q27, Q28, Q29, Q30, Q31, Q32, Q33, Q34, Q35, Q36]), "transformType" : TransformType.TRANSLATION_DISTANCE, "transformDirection" : qUnion([Q37]), "distance" : 12.7 * mm, "oppositeDirection" : true, "makeCopy" : false});
        }
        {
            var Q0;
            Q0=makeQuery(id+"F3.opExtrude","SWEPT_BODY",BODY,{"disambiguationData":[OSD([sQuery(id+"F2.wireOp",EDGE,"E2.sketch_text.stroke-0"),sQuery(id+"F2.wireOp",EDGE,"E2.sketch_text.stroke-1"),sQuery(id+"F2.wireOp",EDGE,"E2.sketch_text.stroke-2"),sQuery(id+"F2.wireOp",EDGE,"E2.sketch_text.stroke-3"),sQuery(id+"F2.wireOp",EDGE,"E2.sketch_text.stroke-4"),sQuery(id+"F2.wireOp",EDGE,"E2.sketch_text.stroke-5"),sQuery(id+"F2.wireOp",EDGE,"E2.sketch_text.stroke-6"),sQuery(id+"F2.wireOp",EDGE,"E2.sketch_text.stroke-7")])]});
            var Q1;
            Q1=makeQuery(id+"F3.opExtrude","SWEPT_BODY",BODY,{"disambiguationData":[OSD([sQuery(id+"F2.wireOp",EDGE,"E2.sketch_text.stroke-8"),sQuery(id+"F2.wireOp",EDGE,"E2.sketch_text.stroke-9"),sQuery(id+"F2.wireOp",EDGE,"E2.sketch_text.stroke-10"),sQuery(id+"F2.wireOp",EDGE,"E2.sketch_text.stroke-11")])]});
            var Q2;
            Q2=makeQuery(id+"F3.opExtrude","SWEPT_BODY",BODY,{"disambiguationData":[OSD([sQuery(id+"F2.wireOp",EDGE,"E2.sketch_text.stroke-12"),sQuery(id+"F2.wireOp",EDGE,"E2.sketch_text.stroke-13"),sQuery(id+"F2.wireOp",EDGE,"E2.sketch_text.stroke-14"),sQuery(id+"F2.wireOp",EDGE,"E2.sketch_text.stroke-15"),sQuery(id+"F2.wireOp",EDGE,"E2.sketch_text.stroke-16"),sQuery(id+"F2.wireOp",EDGE,"E2.sketch_text.stroke-17"),sQuery(id+"F2.wireOp",EDGE,"E2.sketch_text.stroke-18"),sQuery(id+"F2.wireOp",EDGE,"E2.sketch_text.stroke-19"),sQuery(id+"F2.wireOp",EDGE,"E2.sketch_text.stroke-20"),sQuery(id+"F2.wireOp",EDGE,"E2.sketch_text.stroke-21"),sQuery(id+"F2.wireOp",EDGE,"E2.sketch_text.stroke-22"),sQuery(id+"F2.wireOp",EDGE,"E2.sketch_text.stroke-23"),sQuery(id+"F2.wireOp",EDGE,"E2.sketch_text.stroke-24"),sQuery(id+"F2.wireOp",EDGE,"E2.sketch_text.stroke-25"),sQuery(id+"F2.wireOp",EDGE,"E2.sketch_text.stroke-26"),sQuery(id+"F2.wireOp",EDGE,"E2.sketch_text.stroke-27"),sQuery(id+"F2.wireOp",EDGE,"E2.sketch_text.stroke-28"),sQuery(id+"F2.wireOp",EDGE,"E2.sketch_text.stroke-29"),sQuery(id+"F2.wireOp",EDGE,"E2.sketch_text.stroke-30")])]});
            var Q3;
            Q3=makeQuery(id+"F3.opExtrude","SWEPT_BODY",BODY,{"disambiguationData":[OSD([sQuery(id+"F2.wireOp",EDGE,"E2.sketch_text.stroke-31"),sQuery(id+"F2.wireOp",EDGE,"E2.sketch_text.stroke-32"),sQuery(id+"F2.wireOp",EDGE,"E2.sketch_text.stroke-33"),sQuery(id+"F2.wireOp",EDGE,"E2.sketch_text.stroke-34")])]});
            var Q4;
            Q4=makeQuery(id+"F3.opExtrude","SWEPT_BODY",BODY,{"disambiguationData":[OSD([sQuery(id+"F2.wireOp",EDGE,"E2.sketch_text.stroke-35"),sQuery(id+"F2.wireOp",EDGE,"E2.sketch_text.stroke-36"),sQuery(id+"F2.wireOp",EDGE,"E2.sketch_text.stroke-37"),sQuery(id+"F2.wireOp",EDGE,"E2.sketch_text.stroke-38"),sQuery(id+"F2.wireOp",EDGE,"E2.sketch_text.stroke-39"),sQuery(id+"F2.wireOp",EDGE,"E2.sketch_text.stroke-40"),sQuery(id+"F2.wireOp",EDGE,"E2.sketch_text.stroke-41"),sQuery(id+"F2.wireOp",EDGE,"E2.sketch_text.stroke-42")])]});
            var Q5;
            Q5=makeQuery(id+"F3.opExtrude","SWEPT_BODY",BODY,{"disambiguationData":[OSD([sQuery(id+"F2.wireOp",EDGE,"E2.sketch_text.stroke-43"),sQuery(id+"F2.wireOp",EDGE,"E2.sketch_text.stroke-44"),sQuery(id+"F2.wireOp",EDGE,"E2.sketch_text.stroke-45"),sQuery(id+"F2.wireOp",EDGE,"E2.sketch_text.stroke-46"),sQuery(id+"F2.wireOp",EDGE,"E2.sketch_text.stroke-47"),sQuery(id+"F2.wireOp",EDGE,"E2.sketch_text.stroke-48"),sQuery(id+"F2.wireOp",EDGE,"E2.sketch_text.stroke-49"),sQuery(id+"F2.wireOp",EDGE,"E2.sketch_text.stroke-50"),sQuery(id+"F2.wireOp",EDGE,"E2.sketch_text.stroke-51"),sQuery(id+"F2.wireOp",EDGE,"E2.sketch_text.stroke-52"),sQuery(id+"F2.wireOp",EDGE,"E2.sketch_text.stroke-53"),sQuery(id+"F2.wireOp",EDGE,"E2.sketch_text.stroke-54"),sQuery(id+"F2.wireOp",EDGE,"E2.sketch_text.stroke-55"),sQuery(id+"F2.wireOp",EDGE,"E2.sketch_text.stroke-56")])]});
            var Q6;
            Q6=makeQuery(id+"F3.opExtrude","SWEPT_BODY",BODY,{"disambiguationData":[OSD([sQuery(id+"F2.wireOp",EDGE,"E2.sketch_text.stroke-57"),sQuery(id+"F2.wireOp",EDGE,"E2.sketch_text.stroke-58"),sQuery(id+"F2.wireOp",EDGE,"E2.sketch_text.stroke-59"),sQuery(id+"F2.wireOp",EDGE,"E2.sketch_text.stroke-60"),sQuery(id+"F2.wireOp",EDGE,"E2.sketch_text.stroke-61"),sQuery(id+"F2.wireOp",EDGE,"E2.sketch_text.stroke-62")])]});
            var Q7;
            Q7=makeQuery(id+"F3.opExtrude","SWEPT_BODY",BODY,{"disambiguationData":[OSD([sQuery(id+"F2.wireOp",EDGE,"E2.sketch_text.stroke-63"),sQuery(id+"F2.wireOp",EDGE,"E2.sketch_text.stroke-64"),sQuery(id+"F2.wireOp",EDGE,"E2.sketch_text.stroke-65"),sQuery(id+"F2.wireOp",EDGE,"E2.sketch_text.stroke-66"),sQuery(id+"F2.wireOp",EDGE,"E2.sketch_text.stroke-67"),sQuery(id+"F2.wireOp",EDGE,"E2.sketch_text.stroke-68"),sQuery(id+"F2.wireOp",EDGE,"E2.sketch_text.stroke-69"),sQuery(id+"F2.wireOp",EDGE,"E2.sketch_text.stroke-70"),sQuery(id+"F2.wireOp",EDGE,"E2.sketch_text.stroke-71")])]});
            var Q8;
            Q8=makeQuery(id+"F3.opExtrude","SWEPT_BODY",BODY,{"disambiguationData":[OSD([sQuery(id+"F2.wireOp",EDGE,"E2.sketch_text.stroke-72"),sQuery(id+"F2.wireOp",EDGE,"E2.sketch_text.stroke-73"),sQuery(id+"F2.wireOp",EDGE,"E2.sketch_text.stroke-74"),sQuery(id+"F2.wireOp",EDGE,"E2.sketch_text.stroke-75"),sQuery(id+"F2.wireOp",EDGE,"E2.sketch_text.stroke-76"),sQuery(id+"F2.wireOp",EDGE,"E2.sketch_text.stroke-77"),sQuery(id+"F2.wireOp",EDGE,"E2.sketch_text.stroke-78"),sQuery(id+"F2.wireOp",EDGE,"E2.sketch_text.stroke-79"),sQuery(id+"F2.wireOp",EDGE,"E2.sketch_text.stroke-80"),sQuery(id+"F2.wireOp",EDGE,"E2.sketch_text.stroke-81"),sQuery(id+"F2.wireOp",EDGE,"E2.sketch_text.stroke-82"),sQuery(id+"F2.wireOp",EDGE,"E2.sketch_text.stroke-83"),sQuery(id+"F2.wireOp",EDGE,"E2.sketch_text.stroke-84"),sQuery(id+"F2.wireOp",EDGE,"E2.sketch_text.stroke-85")])]});
            var Q9;
            Q9=makeQuery(id+"F3.opExtrude","SWEPT_BODY",BODY,{"disambiguationData":[OSD([sQuery(id+"F2.wireOp",EDGE,"E2.sketch_text.stroke-86"),sQuery(id+"F2.wireOp",EDGE,"E2.sketch_text.stroke-87"),sQuery(id+"F2.wireOp",EDGE,"E2.sketch_text.stroke-88"),sQuery(id+"F2.wireOp",EDGE,"E2.sketch_text.stroke-89")])]});
            var Q10;
            Q10=makeQuery(id+"F3.opExtrude","SWEPT_BODY",BODY,{"disambiguationData":[OSD([sQuery(id+"F2.wireOp",EDGE,"E2.sketch_text.stroke-90"),sQuery(id+"F2.wireOp",EDGE,"E2.sketch_text.stroke-91"),sQuery(id+"F2.wireOp",EDGE,"E2.sketch_text.stroke-92"),sQuery(id+"F2.wireOp",EDGE,"E2.sketch_text.stroke-93"),sQuery(id+"F2.wireOp",EDGE,"E2.sketch_text.stroke-94"),sQuery(id+"F2.wireOp",EDGE,"E2.sketch_text.stroke-95"),sQuery(id+"F2.wireOp",EDGE,"E2.sketch_text.stroke-96"),sQuery(id+"F2.wireOp",EDGE,"E2.sketch_text.stroke-97")])]});
            var Q11;
            Q11=makeQuery(id+"F3.opExtrude","SWEPT_BODY",BODY,{"disambiguationData":[OSD([sQuery(id+"F2.wireOp",EDGE,"E2.sketch_text.stroke-98"),sQuery(id+"F2.wireOp",EDGE,"E2.sketch_text.stroke-99"),sQuery(id+"F2.wireOp",EDGE,"E2.sketch_text.stroke-100"),sQuery(id+"F2.wireOp",EDGE,"E2.sketch_text.stroke-101"),sQuery(id+"F2.wireOp",EDGE,"E2.sketch_text.stroke-102"),sQuery(id+"F2.wireOp",EDGE,"E2.sketch_text.stroke-103"),sQuery(id+"F2.wireOp",EDGE,"E2.sketch_text.stroke-104"),sQuery(id+"F2.wireOp",EDGE,"E2.sketch_text.stroke-105"),sQuery(id+"F2.wireOp",EDGE,"E2.sketch_text.stroke-106"),sQuery(id+"F2.wireOp",EDGE,"E2.sketch_text.stroke-107"),sQuery(id+"F2.wireOp",EDGE,"E2.sketch_text.stroke-108"),sQuery(id+"F2.wireOp",EDGE,"E2.sketch_text.stroke-109"),sQuery(id+"F2.wireOp",EDGE,"E2.sketch_text.stroke-110"),sQuery(id+"F2.wireOp",EDGE,"E2.sketch_text.stroke-111")])]});
            var Q12;
            Q12=makeQuery(id+"F3.opExtrude","SWEPT_BODY",BODY,{"disambiguationData":[OSD([sQuery(id+"F2.wireOp",EDGE,"E2.sketch_text.stroke-112"),sQuery(id+"F2.wireOp",EDGE,"E2.sketch_text.stroke-113"),sQuery(id+"F2.wireOp",EDGE,"E2.sketch_text.stroke-114"),sQuery(id+"F2.wireOp",EDGE,"E2.sketch_text.stroke-115"),sQuery(id+"F2.wireOp",EDGE,"E2.sketch_text.stroke-116"),sQuery(id+"F2.wireOp",EDGE,"E2.sketch_text.stroke-117")])]});
            var Q13;
            Q13=makeQuery(id+"F3.opExtrude","SWEPT_BODY",BODY,{"disambiguationData":[OSD([sQuery(id+"F2.wireOp",EDGE,"E2.sketch_text.stroke-118"),sQuery(id+"F2.wireOp",EDGE,"E2.sketch_text.stroke-119"),sQuery(id+"F2.wireOp",EDGE,"E2.sketch_text.stroke-120"),sQuery(id+"F2.wireOp",EDGE,"E2.sketch_text.stroke-121"),sQuery(id+"F2.wireOp",EDGE,"E2.sketch_text.stroke-122"),sQuery(id+"F2.wireOp",EDGE,"E2.sketch_text.stroke-123"),sQuery(id+"F2.wireOp",EDGE,"E2.sketch_text.stroke-124"),sQuery(id+"F2.wireOp",EDGE,"E2.sketch_text.stroke-125"),sQuery(id+"F2.wireOp",EDGE,"E2.sketch_text.stroke-126")])]});
            var Q14;
            Q14=makeQuery(id+"F3.opExtrude","SWEPT_BODY",BODY,{"disambiguationData":[OSD([sQuery(id+"F2.wireOp",EDGE,"E2.sketch_text.stroke-127"),sQuery(id+"F2.wireOp",EDGE,"E2.sketch_text.stroke-128"),sQuery(id+"F2.wireOp",EDGE,"E2.sketch_text.stroke-129"),sQuery(id+"F2.wireOp",EDGE,"E2.sketch_text.stroke-130"),sQuery(id+"F2.wireOp",EDGE,"E2.sketch_text.stroke-131"),sQuery(id+"F2.wireOp",EDGE,"E2.sketch_text.stroke-132"),sQuery(id+"F2.wireOp",EDGE,"E2.sketch_text.stroke-133"),sQuery(id+"F2.wireOp",EDGE,"E2.sketch_text.stroke-134"),sQuery(id+"F2.wireOp",EDGE,"E2.sketch_text.stroke-135"),sQuery(id+"F2.wireOp",EDGE,"E2.sketch_text.stroke-136"),sQuery(id+"F2.wireOp",EDGE,"E2.sketch_text.stroke-137"),sQuery(id+"F2.wireOp",EDGE,"E2.sketch_text.stroke-138"),sQuery(id+"F2.wireOp",EDGE,"E2.sketch_text.stroke-139"),sQuery(id+"F2.wireOp",EDGE,"E2.sketch_text.stroke-140")])]});
            var Q15;
            Q15=makeQuery(id+"F3.opExtrude","SWEPT_BODY",BODY,{"disambiguationData":[OSD([sQuery(id+"F2.wireOp",EDGE,"E2.sketch_text.stroke-141"),sQuery(id+"F2.wireOp",EDGE,"E2.sketch_text.stroke-142"),sQuery(id+"F2.wireOp",EDGE,"E2.sketch_text.stroke-143"),sQuery(id+"F2.wireOp",EDGE,"E2.sketch_text.stroke-144"),sQuery(id+"F2.wireOp",EDGE,"E2.sketch_text.stroke-145")])]});
            var Q16;
            Q16=makeQuery(id+"F3.opExtrude","SWEPT_BODY",BODY,{"disambiguationData":[OSD([sQuery(id+"F2.wireOp",EDGE,"E2.sketch_text.stroke-146"),sQuery(id+"F2.wireOp",EDGE,"E2.sketch_text.stroke-147"),sQuery(id+"F2.wireOp",EDGE,"E2.sketch_text.stroke-148"),sQuery(id+"F2.wireOp",EDGE,"E2.sketch_text.stroke-149"),sQuery(id+"F2.wireOp",EDGE,"E2.sketch_text.stroke-150"),sQuery(id+"F2.wireOp",EDGE,"E2.sketch_text.stroke-151"),sQuery(id+"F2.wireOp",EDGE,"E2.sketch_text.stroke-152"),sQuery(id+"F2.wireOp",EDGE,"E2.sketch_text.stroke-153"),sQuery(id+"F2.wireOp",EDGE,"E2.sketch_text.stroke-154"),sQuery(id+"F2.wireOp",EDGE,"E2.sketch_text.stroke-155"),sQuery(id+"F2.wireOp",EDGE,"E2.sketch_text.stroke-156"),sQuery(id+"F2.wireOp",EDGE,"E2.sketch_text.stroke-157"),sQuery(id+"F2.wireOp",EDGE,"E2.sketch_text.stroke-158"),sQuery(id+"F2.wireOp",EDGE,"E2.sketch_text.stroke-159"),sQuery(id+"F2.wireOp",EDGE,"E2.sketch_text.stroke-160"),sQuery(id+"F2.wireOp",EDGE,"E2.sketch_text.stroke-161")])]});
            var Q17;
            Q17=makeQuery(id+"F3.opExtrude","SWEPT_BODY",BODY,{"disambiguationData":[OSD([sQuery(id+"F2.wireOp",EDGE,"E2.sketch_text.stroke-162"),sQuery(id+"F2.wireOp",EDGE,"E2.sketch_text.stroke-163"),sQuery(id+"F2.wireOp",EDGE,"E2.sketch_text.stroke-164"),sQuery(id+"F2.wireOp",EDGE,"E2.sketch_text.stroke-165"),sQuery(id+"F2.wireOp",EDGE,"E2.sketch_text.stroke-166"),sQuery(id+"F2.wireOp",EDGE,"E2.sketch_text.stroke-167"),sQuery(id+"F2.wireOp",EDGE,"E2.sketch_text.stroke-168"),sQuery(id+"F2.wireOp",EDGE,"E2.sketch_text.stroke-169"),sQuery(id+"F2.wireOp",EDGE,"E2.sketch_text.stroke-170"),sQuery(id+"F2.wireOp",EDGE,"E2.sketch_text.stroke-171"),sQuery(id+"F2.wireOp",EDGE,"E2.sketch_text.stroke-172"),sQuery(id+"F2.wireOp",EDGE,"E2.sketch_text.stroke-173"),sQuery(id+"F2.wireOp",EDGE,"E2.sketch_text.stroke-174"),sQuery(id+"F2.wireOp",EDGE,"E2.sketch_text.stroke-175"),sQuery(id+"F2.wireOp",EDGE,"E2.sketch_text.stroke-176"),sQuery(id+"F2.wireOp",EDGE,"E2.sketch_text.stroke-177"),sQuery(id+"F2.wireOp",EDGE,"E2.sketch_text.stroke-178"),sQuery(id+"F2.wireOp",EDGE,"E2.sketch_text.stroke-179")])]});
            var Q18;
            Q18=makeQuery(id+"F3.opExtrude","SWEPT_BODY",BODY,{"disambiguationData":[OSD([sQuery(id+"F2.wireOp",EDGE,"E2.sketch_text.stroke-180"),sQuery(id+"F2.wireOp",EDGE,"E2.sketch_text.stroke-181"),sQuery(id+"F2.wireOp",EDGE,"E2.sketch_text.stroke-182"),sQuery(id+"F2.wireOp",EDGE,"E2.sketch_text.stroke-183"),sQuery(id+"F2.wireOp",EDGE,"E2.sketch_text.stroke-184"),sQuery(id+"F2.wireOp",EDGE,"E2.sketch_text.stroke-185"),sQuery(id+"F2.wireOp",EDGE,"E2.sketch_text.stroke-186"),sQuery(id+"F2.wireOp",EDGE,"E2.sketch_text.stroke-187"),sQuery(id+"F2.wireOp",EDGE,"E2.sketch_text.stroke-188"),sQuery(id+"F2.wireOp",EDGE,"E2.sketch_text.stroke-189"),sQuery(id+"F2.wireOp",EDGE,"E2.sketch_text.stroke-190"),sQuery(id+"F2.wireOp",EDGE,"E2.sketch_text.stroke-191"),sQuery(id+"F2.wireOp",EDGE,"E2.sketch_text.stroke-192"),sQuery(id+"F2.wireOp",EDGE,"E2.sketch_text.stroke-193"),sQuery(id+"F2.wireOp",EDGE,"E2.sketch_text.stroke-194"),sQuery(id+"F2.wireOp",EDGE,"E2.sketch_text.stroke-195"),sQuery(id+"F2.wireOp",EDGE,"E2.sketch_text.stroke-196"),sQuery(id+"F2.wireOp",EDGE,"E2.sketch_text.stroke-197"),sQuery(id+"F2.wireOp",EDGE,"E2.sketch_text.stroke-198"),sQuery(id+"F2.wireOp",EDGE,"E2.sketch_text.stroke-199"),sQuery(id+"F2.wireOp",EDGE,"E2.sketch_text.stroke-200"),sQuery(id+"F2.wireOp",EDGE,"E2.sketch_text.stroke-201"),sQuery(id+"F2.wireOp",EDGE,"E2.sketch_text.stroke-202"),sQuery(id+"F2.wireOp",EDGE,"E2.sketch_text.stroke-203")])]});
            var Q19;
            Q19=makeQuery(id+"F3.opExtrude","SWEPT_BODY",BODY,{"disambiguationData":[OSD([sQuery(id+"F2.wireOp",EDGE,"E2.sketch_text.stroke-204"),sQuery(id+"F2.wireOp",EDGE,"E2.sketch_text.stroke-205"),sQuery(id+"F2.wireOp",EDGE,"E2.sketch_text.stroke-206"),sQuery(id+"F2.wireOp",EDGE,"E2.sketch_text.stroke-207"),sQuery(id+"F2.wireOp",EDGE,"E2.sketch_text.stroke-208")])]});
            var Q20;
            Q20=makeQuery(id+"F3.opExtrude","SWEPT_BODY",BODY,{"disambiguationData":[OSD([sQuery(id+"F2.wireOp",EDGE,"E2.sketch_text.stroke-209"),sQuery(id+"F2.wireOp",EDGE,"E2.sketch_text.stroke-210"),sQuery(id+"F2.wireOp",EDGE,"E2.sketch_text.stroke-211"),sQuery(id+"F2.wireOp",EDGE,"E2.sketch_text.stroke-212"),sQuery(id+"F2.wireOp",EDGE,"E2.sketch_text.stroke-213"),sQuery(id+"F2.wireOp",EDGE,"E2.sketch_text.stroke-214"),sQuery(id+"F2.wireOp",EDGE,"E2.sketch_text.stroke-215"),sQuery(id+"F2.wireOp",EDGE,"E2.sketch_text.stroke-216"),sQuery(id+"F2.wireOp",EDGE,"E2.sketch_text.stroke-217"),sQuery(id+"F2.wireOp",EDGE,"E2.sketch_text.stroke-218"),sQuery(id+"F2.wireOp",EDGE,"E2.sketch_text.stroke-219"),sQuery(id+"F2.wireOp",EDGE,"E2.sketch_text.stroke-220"),sQuery(id+"F2.wireOp",EDGE,"E2.sketch_text.stroke-221"),sQuery(id+"F2.wireOp",EDGE,"E2.sketch_text.stroke-222"),sQuery(id+"F2.wireOp",EDGE,"E2.sketch_text.stroke-223"),sQuery(id+"F2.wireOp",EDGE,"E2.sketch_text.stroke-224"),sQuery(id+"F2.wireOp",EDGE,"E2.sketch_text.stroke-225"),sQuery(id+"F2.wireOp",EDGE,"E2.sketch_text.stroke-226")])]});
            var Q21;
            Q21=makeQuery(id+"F3.opExtrude","SWEPT_BODY",BODY,{"disambiguationData":[OSD([sQuery(id+"F2.wireOp",EDGE,"E2.sketch_text.stroke-227"),sQuery(id+"F2.wireOp",EDGE,"E2.sketch_text.stroke-228"),sQuery(id+"F2.wireOp",EDGE,"E2.sketch_text.stroke-229"),sQuery(id+"F2.wireOp",EDGE,"E2.sketch_text.stroke-230"),sQuery(id+"F2.wireOp",EDGE,"E2.sketch_text.stroke-231"),sQuery(id+"F2.wireOp",EDGE,"E2.sketch_text.stroke-232"),sQuery(id+"F2.wireOp",EDGE,"E2.sketch_text.stroke-233"),sQuery(id+"F2.wireOp",EDGE,"E2.sketch_text.stroke-234"),sQuery(id+"F2.wireOp",EDGE,"E2.sketch_text.stroke-235"),sQuery(id+"F2.wireOp",EDGE,"E2.sketch_text.stroke-236"),sQuery(id+"F2.wireOp",EDGE,"E2.sketch_text.stroke-237"),sQuery(id+"F2.wireOp",EDGE,"E2.sketch_text.stroke-238"),sQuery(id+"F2.wireOp",EDGE,"E2.sketch_text.stroke-239")])]});
            var Q22;
            Q22=makeQuery(id+"F3.opExtrude","SWEPT_BODY",BODY,{"disambiguationData":[OSD([sQuery(id+"F2.wireOp",EDGE,"E2.sketch_text.stroke-240"),sQuery(id+"F2.wireOp",EDGE,"E2.sketch_text.stroke-241"),sQuery(id+"F2.wireOp",EDGE,"E2.sketch_text.stroke-242"),sQuery(id+"F2.wireOp",EDGE,"E2.sketch_text.stroke-243"),sQuery(id+"F2.wireOp",EDGE,"E2.sketch_text.stroke-244"),sQuery(id+"F2.wireOp",EDGE,"E2.sketch_text.stroke-245"),sQuery(id+"F2.wireOp",EDGE,"E2.sketch_text.stroke-246"),sQuery(id+"F2.wireOp",EDGE,"E2.sketch_text.stroke-247"),sQuery(id+"F2.wireOp",EDGE,"E2.sketch_text.stroke-248"),sQuery(id+"F2.wireOp",EDGE,"E2.sketch_text.stroke-249"),sQuery(id+"F2.wireOp",EDGE,"E2.sketch_text.stroke-250"),sQuery(id+"F2.wireOp",EDGE,"E2.sketch_text.stroke-251"),sQuery(id+"F2.wireOp",EDGE,"E2.sketch_text.stroke-252"),sQuery(id+"F2.wireOp",EDGE,"E2.sketch_text.stroke-253"),sQuery(id+"F2.wireOp",EDGE,"E2.sketch_text.stroke-254"),sQuery(id+"F2.wireOp",EDGE,"E2.sketch_text.stroke-255"),sQuery(id+"F2.wireOp",EDGE,"E2.sketch_text.stroke-256"),sQuery(id+"F2.wireOp",EDGE,"E2.sketch_text.stroke-257"),sQuery(id+"F2.wireOp",EDGE,"E2.sketch_text.stroke-258"),sQuery(id+"F2.wireOp",EDGE,"E2.sketch_text.stroke-259"),sQuery(id+"F2.wireOp",EDGE,"E2.sketch_text.stroke-260"),sQuery(id+"F2.wireOp",EDGE,"E2.sketch_text.stroke-261"),sQuery(id+"F2.wireOp",EDGE,"E2.sketch_text.stroke-262"),sQuery(id+"F2.wireOp",EDGE,"E2.sketch_text.stroke-263")])]});
            var Q23;
            Q23=makeQuery(id+"F3.opExtrude","SWEPT_BODY",BODY,{"disambiguationData":[OSD([sQuery(id+"F2.wireOp",EDGE,"E2.sketch_text.stroke-264"),sQuery(id+"F2.wireOp",EDGE,"E2.sketch_text.stroke-265"),sQuery(id+"F2.wireOp",EDGE,"E2.sketch_text.stroke-266"),sQuery(id+"F2.wireOp",EDGE,"E2.sketch_text.stroke-267"),sQuery(id+"F2.wireOp",EDGE,"E2.sketch_text.stroke-268"),sQuery(id+"F2.wireOp",EDGE,"E2.sketch_text.stroke-269"),sQuery(id+"F2.wireOp",EDGE,"E2.sketch_text.stroke-270"),sQuery(id+"F2.wireOp",EDGE,"E2.sketch_text.stroke-271"),sQuery(id+"F2.wireOp",EDGE,"E2.sketch_text.stroke-272"),sQuery(id+"F2.wireOp",EDGE,"E2.sketch_text.stroke-273"),sQuery(id+"F2.wireOp",EDGE,"E2.sketch_text.stroke-274"),sQuery(id+"F2.wireOp",EDGE,"E2.sketch_text.stroke-275"),sQuery(id+"F2.wireOp",EDGE,"E2.sketch_text.stroke-276"),sQuery(id+"F2.wireOp",EDGE,"E2.sketch_text.stroke-277"),sQuery(id+"F2.wireOp",EDGE,"E2.sketch_text.stroke-278"),sQuery(id+"F2.wireOp",EDGE,"E2.sketch_text.stroke-279"),sQuery(id+"F2.wireOp",EDGE,"E2.sketch_text.stroke-280"),sQuery(id+"F2.wireOp",EDGE,"E2.sketch_text.stroke-281"),sQuery(id+"F2.wireOp",EDGE,"E2.sketch_text.stroke-282"),sQuery(id+"F2.wireOp",EDGE,"E2.sketch_text.stroke-283"),sQuery(id+"F2.wireOp",EDGE,"E2.sketch_text.stroke-284"),sQuery(id+"F2.wireOp",EDGE,"E2.sketch_text.stroke-285"),sQuery(id+"F2.wireOp",EDGE,"E2.sketch_text.stroke-286"),sQuery(id+"F2.wireOp",EDGE,"E2.sketch_text.stroke-287"),sQuery(id+"F2.wireOp",EDGE,"E2.sketch_text.stroke-288")])]});
            var Q24;
            Q24=makeQuery(id+"F3.opExtrude","SWEPT_BODY",BODY,{"disambiguationData":[OSD([sQuery(id+"F2.wireOp",EDGE,"E2.sketch_text.stroke-289"),sQuery(id+"F2.wireOp",EDGE,"E2.sketch_text.stroke-290"),sQuery(id+"F2.wireOp",EDGE,"E2.sketch_text.stroke-291"),sQuery(id+"F2.wireOp",EDGE,"E2.sketch_text.stroke-292"),sQuery(id+"F2.wireOp",EDGE,"E2.sketch_text.stroke-293"),sQuery(id+"F2.wireOp",EDGE,"E2.sketch_text.stroke-294"),sQuery(id+"F2.wireOp",EDGE,"E2.sketch_text.stroke-295"),sQuery(id+"F2.wireOp",EDGE,"E2.sketch_text.stroke-296"),sQuery(id+"F2.wireOp",EDGE,"E2.sketch_text.stroke-297"),sQuery(id+"F2.wireOp",EDGE,"E2.sketch_text.stroke-298"),sQuery(id+"F2.wireOp",EDGE,"E2.sketch_text.stroke-299"),sQuery(id+"F2.wireOp",EDGE,"E2.sketch_text.stroke-300"),sQuery(id+"F2.wireOp",EDGE,"E2.sketch_text.stroke-301"),sQuery(id+"F2.wireOp",EDGE,"E2.sketch_text.stroke-302"),sQuery(id+"F2.wireOp",EDGE,"E2.sketch_text.stroke-303"),sQuery(id+"F2.wireOp",EDGE,"E2.sketch_text.stroke-304"),sQuery(id+"F2.wireOp",EDGE,"E2.sketch_text.stroke-305"),sQuery(id+"F2.wireOp",EDGE,"E2.sketch_text.stroke-306"),sQuery(id+"F2.wireOp",EDGE,"E2.sketch_text.stroke-307"),sQuery(id+"F2.wireOp",EDGE,"E2.sketch_text.stroke-308"),sQuery(id+"F2.wireOp",EDGE,"E2.sketch_text.stroke-309"),sQuery(id+"F2.wireOp",EDGE,"E2.sketch_text.stroke-310"),sQuery(id+"F2.wireOp",EDGE,"E2.sketch_text.stroke-311"),sQuery(id+"F2.wireOp",EDGE,"E2.sketch_text.stroke-312"),sQuery(id+"F2.wireOp",EDGE,"E2.sketch_text.stroke-313")])]});
            var Q25;
            Q25=makeQuery(id+"F3.opExtrude","SWEPT_BODY",BODY,{"disambiguationData":[OSD([sQuery(id+"F2.wireOp",EDGE,"E2.sketch_text.stroke-314"),sQuery(id+"F2.wireOp",EDGE,"E2.sketch_text.stroke-315"),sQuery(id+"F2.wireOp",EDGE,"E2.sketch_text.stroke-316"),sQuery(id+"F2.wireOp",EDGE,"E2.sketch_text.stroke-317"),sQuery(id+"F2.wireOp",EDGE,"E2.sketch_text.stroke-318"),sQuery(id+"F2.wireOp",EDGE,"E2.sketch_text.stroke-319"),sQuery(id+"F2.wireOp",EDGE,"E2.sketch_text.stroke-320"),sQuery(id+"F2.wireOp",EDGE,"E2.sketch_text.stroke-321"),sQuery(id+"F2.wireOp",EDGE,"E2.sketch_text.stroke-322"),sQuery(id+"F2.wireOp",EDGE,"E2.sketch_text.stroke-323"),sQuery(id+"F2.wireOp",EDGE,"E2.sketch_text.stroke-324"),sQuery(id+"F2.wireOp",EDGE,"E2.sketch_text.stroke-325"),sQuery(id+"F2.wireOp",EDGE,"E2.sketch_text.stroke-326")])]});
            var Q26;
            Q26=makeQuery(id+"F3.opExtrude","SWEPT_BODY",BODY,{"disambiguationData":[OSD([sQuery(id+"F2.wireOp",EDGE,"E2.sketch_text.stroke-327"),sQuery(id+"F2.wireOp",EDGE,"E2.sketch_text.stroke-328"),sQuery(id+"F2.wireOp",EDGE,"E2.sketch_text.stroke-329"),sQuery(id+"F2.wireOp",EDGE,"E2.sketch_text.stroke-330"),sQuery(id+"F2.wireOp",EDGE,"E2.sketch_text.stroke-331"),sQuery(id+"F2.wireOp",EDGE,"E2.sketch_text.stroke-332"),sQuery(id+"F2.wireOp",EDGE,"E2.sketch_text.stroke-333"),sQuery(id+"F2.wireOp",EDGE,"E2.sketch_text.stroke-334"),sQuery(id+"F2.wireOp",EDGE,"E2.sketch_text.stroke-335"),sQuery(id+"F2.wireOp",EDGE,"E2.sketch_text.stroke-336"),sQuery(id+"F2.wireOp",EDGE,"E2.sketch_text.stroke-337"),sQuery(id+"F2.wireOp",EDGE,"E2.sketch_text.stroke-338"),sQuery(id+"F2.wireOp",EDGE,"E2.sketch_text.stroke-339"),sQuery(id+"F2.wireOp",EDGE,"E2.sketch_text.stroke-340"),sQuery(id+"F2.wireOp",EDGE,"E2.sketch_text.stroke-341"),sQuery(id+"F2.wireOp",EDGE,"E2.sketch_text.stroke-342"),sQuery(id+"F2.wireOp",EDGE,"E2.sketch_text.stroke-343"),sQuery(id+"F2.wireOp",EDGE,"E2.sketch_text.stroke-344"),sQuery(id+"F2.wireOp",EDGE,"E2.sketch_text.stroke-345"),sQuery(id+"F2.wireOp",EDGE,"E2.sketch_text.stroke-346"),sQuery(id+"F2.wireOp",EDGE,"E2.sketch_text.stroke-347"),sQuery(id+"F2.wireOp",EDGE,"E2.sketch_text.stroke-348"),sQuery(id+"F2.wireOp",EDGE,"E2.sketch_text.stroke-349"),sQuery(id+"F2.wireOp",EDGE,"E2.sketch_text.stroke-350")])]});
            var Q27;
            Q27=makeQuery(id+"F3.opExtrude","SWEPT_BODY",BODY,{"disambiguationData":[OSD([sQuery(id+"F2.wireOp",EDGE,"E2.sketch_text.stroke-351"),sQuery(id+"F2.wireOp",EDGE,"E2.sketch_text.stroke-352"),sQuery(id+"F2.wireOp",EDGE,"E2.sketch_text.stroke-353"),sQuery(id+"F2.wireOp",EDGE,"E2.sketch_text.stroke-354"),sQuery(id+"F2.wireOp",EDGE,"E2.sketch_text.stroke-355"),sQuery(id+"F2.wireOp",EDGE,"E2.sketch_text.stroke-356"),sQuery(id+"F2.wireOp",EDGE,"E2.sketch_text.stroke-357")])]});
            var Q28;
            Q28=makeQuery(id+"F3.opExtrude","SWEPT_BODY",BODY,{"disambiguationData":[OSD([sQuery(id+"F2.wireOp",EDGE,"E2.sketch_text.stroke-358"),sQuery(id+"F2.wireOp",EDGE,"E2.sketch_text.stroke-359"),sQuery(id+"F2.wireOp",EDGE,"E2.sketch_text.stroke-360"),sQuery(id+"F2.wireOp",EDGE,"E2.sketch_text.stroke-361"),sQuery(id+"F2.wireOp",EDGE,"E2.sketch_text.stroke-362"),sQuery(id+"F2.wireOp",EDGE,"E2.sketch_text.stroke-363"),sQuery(id+"F2.wireOp",EDGE,"E2.sketch_text.stroke-364")])]});
            var Q29;
            Q29=makeQuery(id+"F3.opExtrude","SWEPT_BODY",BODY,{"disambiguationData":[OSD([sQuery(id+"F2.wireOp",EDGE,"E2.sketch_text.stroke-365"),sQuery(id+"F2.wireOp",EDGE,"E2.sketch_text.stroke-366"),sQuery(id+"F2.wireOp",EDGE,"E2.sketch_text.stroke-367"),sQuery(id+"F2.wireOp",EDGE,"E2.sketch_text.stroke-368")])]});
            var Q30;
            Q30=makeQuery(id+"F3.opExtrude","SWEPT_BODY",BODY,{"disambiguationData":[OSD([sQuery(id+"F2.wireOp",EDGE,"E2.sketch_text.stroke-369"),sQuery(id+"F2.wireOp",EDGE,"E2.sketch_text.stroke-370"),sQuery(id+"F2.wireOp",EDGE,"E2.sketch_text.stroke-371"),sQuery(id+"F2.wireOp",EDGE,"E2.sketch_text.stroke-372"),sQuery(id+"F2.wireOp",EDGE,"E2.sketch_text.stroke-373"),sQuery(id+"F2.wireOp",EDGE,"E2.sketch_text.stroke-374"),sQuery(id+"F2.wireOp",EDGE,"E2.sketch_text.stroke-375"),sQuery(id+"F2.wireOp",EDGE,"E2.sketch_text.stroke-376")])]});
            var Q31;
            Q31=makeQuery(id+"F3.opExtrude","SWEPT_BODY",BODY,{"disambiguationData":[OSD([sQuery(id+"F2.wireOp",EDGE,"E2.sketch_text.stroke-377"),sQuery(id+"F2.wireOp",EDGE,"E2.sketch_text.stroke-378"),sQuery(id+"F2.wireOp",EDGE,"E2.sketch_text.stroke-379"),sQuery(id+"F2.wireOp",EDGE,"E2.sketch_text.stroke-380"),sQuery(id+"F2.wireOp",EDGE,"E2.sketch_text.stroke-381")])]});
            var Q32;
            Q32=makeQuery(id+"F3.opExtrude","SWEPT_BODY",BODY,{"disambiguationData":[OSD([sQuery(id+"F2.wireOp",EDGE,"E2.sketch_text.stroke-382"),sQuery(id+"F2.wireOp",EDGE,"E2.sketch_text.stroke-383"),sQuery(id+"F2.wireOp",EDGE,"E2.sketch_text.stroke-384"),sQuery(id+"F2.wireOp",EDGE,"E2.sketch_text.stroke-385"),sQuery(id+"F2.wireOp",EDGE,"E2.sketch_text.stroke-386"),sQuery(id+"F2.wireOp",EDGE,"E2.sketch_text.stroke-387"),sQuery(id+"F2.wireOp",EDGE,"E2.sketch_text.stroke-388"),sQuery(id+"F2.wireOp",EDGE,"E2.sketch_text.stroke-389"),sQuery(id+"F2.wireOp",EDGE,"E2.sketch_text.stroke-390"),sQuery(id+"F2.wireOp",EDGE,"E2.sketch_text.stroke-391"),sQuery(id+"F2.wireOp",EDGE,"E2.sketch_text.stroke-392"),sQuery(id+"F2.wireOp",EDGE,"E2.sketch_text.stroke-393"),sQuery(id+"F2.wireOp",EDGE,"E2.sketch_text.stroke-394"),sQuery(id+"F2.wireOp",EDGE,"E2.sketch_text.stroke-395"),sQuery(id+"F2.wireOp",EDGE,"E2.sketch_text.stroke-396"),sQuery(id+"F2.wireOp",EDGE,"E2.sketch_text.stroke-397"),sQuery(id+"F2.wireOp",EDGE,"E2.sketch_text.stroke-398"),sQuery(id+"F2.wireOp",EDGE,"E2.sketch_text.stroke-399"),sQuery(id+"F2.wireOp",EDGE,"E2.sketch_text.stroke-400")])]});
            var Q33;
            Q33=makeQuery(id+"F3.opExtrude","SWEPT_BODY",BODY,{"disambiguationData":[OSD([sQuery(id+"F2.wireOp",EDGE,"E2.sketch_text.stroke-401"),sQuery(id+"F2.wireOp",EDGE,"E2.sketch_text.stroke-402"),sQuery(id+"F2.wireOp",EDGE,"E2.sketch_text.stroke-403"),sQuery(id+"F2.wireOp",EDGE,"E2.sketch_text.stroke-404"),sQuery(id+"F2.wireOp",EDGE,"E2.sketch_text.stroke-405"),sQuery(id+"F2.wireOp",EDGE,"E2.sketch_text.stroke-406"),sQuery(id+"F2.wireOp",EDGE,"E2.sketch_text.stroke-407"),sQuery(id+"F2.wireOp",EDGE,"E2.sketch_text.stroke-408"),sQuery(id+"F2.wireOp",EDGE,"E2.sketch_text.stroke-409"),sQuery(id+"F2.wireOp",EDGE,"E2.sketch_text.stroke-410"),sQuery(id+"F2.wireOp",EDGE,"E2.sketch_text.stroke-411"),sQuery(id+"F2.wireOp",EDGE,"E2.sketch_text.stroke-412"),sQuery(id+"F2.wireOp",EDGE,"E2.sketch_text.stroke-413"),sQuery(id+"F2.wireOp",EDGE,"E2.sketch_text.stroke-414"),sQuery(id+"F2.wireOp",EDGE,"E2.sketch_text.stroke-415"),sQuery(id+"F2.wireOp",EDGE,"E2.sketch_text.stroke-416"),sQuery(id+"F2.wireOp",EDGE,"E2.sketch_text.stroke-417"),sQuery(id+"F2.wireOp",EDGE,"E2.sketch_text.stroke-418"),sQuery(id+"F2.wireOp",EDGE,"E2.sketch_text.stroke-419"),sQuery(id+"F2.wireOp",EDGE,"E2.sketch_text.stroke-420"),sQuery(id+"F2.wireOp",EDGE,"E2.sketch_text.stroke-421"),sQuery(id+"F2.wireOp",EDGE,"E2.sketch_text.stroke-422"),sQuery(id+"F2.wireOp",EDGE,"E2.sketch_text.stroke-423"),sQuery(id+"F2.wireOp",EDGE,"E2.sketch_text.stroke-424"),sQuery(id+"F2.wireOp",EDGE,"E2.sketch_text.stroke-425"),sQuery(id+"F2.wireOp",EDGE,"E2.sketch_text.stroke-426")])]});
            var Q34;
            Q34=makeQuery(id+"F3.opExtrude","SWEPT_BODY",BODY,{"disambiguationData":[OSD([sQuery(id+"F2.wireOp",EDGE,"E2.sketch_text.stroke-427"),sQuery(id+"F2.wireOp",EDGE,"E2.sketch_text.stroke-428"),sQuery(id+"F2.wireOp",EDGE,"E2.sketch_text.stroke-429"),sQuery(id+"F2.wireOp",EDGE,"E2.sketch_text.stroke-430"),sQuery(id+"F2.wireOp",EDGE,"E2.sketch_text.stroke-431"),sQuery(id+"F2.wireOp",EDGE,"E2.sketch_text.stroke-432"),sQuery(id+"F2.wireOp",EDGE,"E2.sketch_text.stroke-433"),sQuery(id+"F2.wireOp",EDGE,"E2.sketch_text.stroke-434"),sQuery(id+"F2.wireOp",EDGE,"E2.sketch_text.stroke-435"),sQuery(id+"F2.wireOp",EDGE,"E2.sketch_text.stroke-436"),sQuery(id+"F2.wireOp",EDGE,"E2.sketch_text.stroke-437"),sQuery(id+"F2.wireOp",EDGE,"E2.sketch_text.stroke-438"),sQuery(id+"F2.wireOp",EDGE,"E2.sketch_text.stroke-439"),sQuery(id+"F2.wireOp",EDGE,"E2.sketch_text.stroke-440"),sQuery(id+"F2.wireOp",EDGE,"E2.sketch_text.stroke-441"),sQuery(id+"F2.wireOp",EDGE,"E2.sketch_text.stroke-442"),sQuery(id+"F2.wireOp",EDGE,"E2.sketch_text.stroke-443")])]});
            var Q35;
            Q35=makeQuery(id+"F3.opExtrude","SWEPT_BODY",BODY,{"disambiguationData":[OSD([sQuery(id+"F2.wireOp",EDGE,"E2.sketch_text.stroke-444"),sQuery(id+"F2.wireOp",EDGE,"E2.sketch_text.stroke-445"),sQuery(id+"F2.wireOp",EDGE,"E2.sketch_text.stroke-446"),sQuery(id+"F2.wireOp",EDGE,"E2.sketch_text.stroke-447")])]});
            var Q36;
            Q36=makeQuery(id+"F3.opExtrude","SWEPT_BODY",BODY,{"disambiguationData":[OSD([sQuery(id+"F2.wireOp",EDGE,"E2.sketch_text.stroke-448"),sQuery(id+"F2.wireOp",EDGE,"E2.sketch_text.stroke-449"),sQuery(id+"F2.wireOp",EDGE,"E2.sketch_text.stroke-450"),sQuery(id+"F2.wireOp",EDGE,"E2.sketch_text.stroke-451"),sQuery(id+"F2.wireOp",EDGE,"E2.sketch_text.stroke-452"),sQuery(id+"F2.wireOp",EDGE,"E2.sketch_text.stroke-453"),sQuery(id+"F2.wireOp",EDGE,"E2.sketch_text.stroke-454"),sQuery(id+"F2.wireOp",EDGE,"E2.sketch_text.stroke-455")])]});
            var Q37;
            Q37=makeQuery(id+"F1.opExtrude","SWEPT_BODY",BODY,{"disambiguationData":[OSD([sQuery(id+"F0.wireOp",EDGE,"E0"),sQuery(id+"F0.wireOp",EDGE,"E1")])]});
            booleanBodies(context, id + "F5", {"operationType" : BooleanOperationType.SUBTRACTION, "tools" : qUnion([Q0, Q1, Q2, Q3, Q4, Q5, Q6, Q7, Q8, Q9, Q10, Q11, Q12, Q13, Q14, Q15, Q16, Q17, Q18, Q19, Q20, Q21, Q22, Q23, Q24, Q25, Q26, Q27, Q28, Q29, Q30, Q31, Q32, Q33, Q34, Q35, Q36]), "targets" : qUnion([Q37])});
        }
    });
